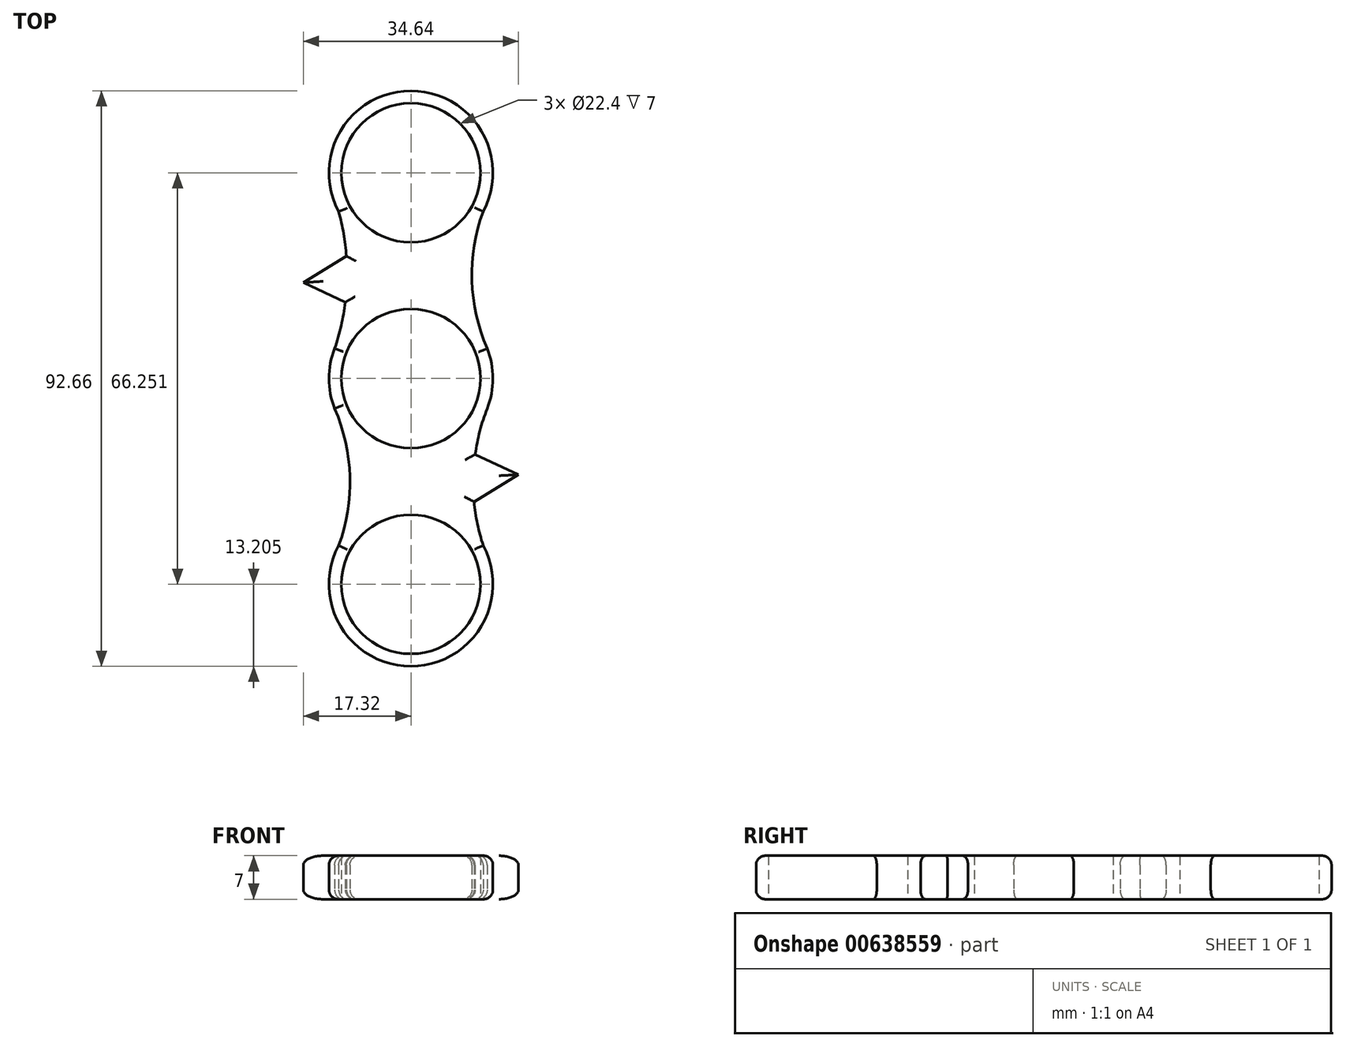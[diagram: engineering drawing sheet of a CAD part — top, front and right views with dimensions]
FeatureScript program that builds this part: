
annotation { "Feature Type Name" : "Feature", "Feature Type Description" : "" }
export const myFeature = defineFeature(function(context is Context, id is Id, definition is map)
    precondition{}
    {
        {
            var Q0;
            Q0=qCreatedBy(makeId("Top.planeOp"),FACE);
            var sketch = newSketch(context, id + "F0", { "sketchPlane" : qUnion([Q0])});
            skCircle(sketch, "E0", {"center": v(0, 0) * mm, "radius": 11.2 * mm});
            skArc(sketch, "E1", {"start": v(12.28, -4.84) * mm, "mid": v(13.2, 0.32) * mm, "end": v(12.03, 5.43) * mm});
            skCircle(sketch, "E2", {"center": v(0, 33.13) * mm, "radius": 11.2 * mm});
            skArc(sketch, "E3", {"start": v(11.63, 26.89) * mm, "mid": v(0, 46.33) * mm, "end": v(-11.63, 26.89) * mm});
            skArc(sketch, "E4.1.0", {"start": v(-11.63, -26.89) * mm, "mid": v(0, -46.33) * mm, "end": v(11.63, -26.89) * mm});
            skCircle(sketch, "E4.1.1", {"center": v(0, -33.13) * mm, "radius": 11.2 * mm});
            skArc(sketch, "E5", {"start": v(11.63, 26.89) * mm, "mid": v(9.83, 15.8) * mm, "end": v(12.28, 4.84) * mm});
            skArc(sketch, "E6.1.0", {"start": v(-11.63, -26.89) * mm, "mid": v(-9.83, -15.8) * mm, "end": v(-12.28, -4.84) * mm});
            skArc(sketch, "E7", {"start": v(-12.28, 4.84) * mm, "mid": v(-11.23, 8.53) * mm, "end": v(-10.57, 12.3) * mm});
            skArc(sketch, "E8", {"start": v(12.28, -4.84) * mm, "mid": v(11.1, -8.46) * mm, "end": v(10.35, -12.2) * mm});
            skArc(sketch, "E9.trimOffspring", {"start": v(-12.28, 4.84) * mm, "mid": v(-13.2, -0.32) * mm, "end": v(-12.03, -5.43) * mm});
            skLineSegment(sketch, "E10", {"start": v(10.35, -12.2) * mm, "end": v(17.32, -15.47) * mm});
            skLineSegment(sketch, "E11", {"start": v(17.32, -15.47) * mm, "end": v(10.17, -19.84) * mm});
            skLineSegment(sketch, "E12.1.0", {"start": v(-17.32, 15.47) * mm, "end": v(-10.17, 19.84) * mm});
            skLineSegment(sketch, "E12.1.1", {"start": v(-10.35, 12.2) * mm, "end": v(-17.32, 15.47) * mm});
            skArc(sketch, "E13.trimOffspring", {"start": v(10.17, -19.84) * mm, "mid": v(10.7, -23.4) * mm, "end": v(11.63, -26.89) * mm});
            skArc(sketch, "E14.trimOffspring", {"start": v(-10.38, 19.7) * mm, "mid": v(-10.83, 23.33) * mm, "end": v(-11.63, 26.89) * mm});
            skSolve(sketch);
        }
        {
            var Q0;
            Q0=makeQuery(id+"F0.imprint","IMPRINT",FACE,{"disambiguationData":[TD([[makeQuery(id+"F0.imprint","IMPRINT",EDGE,{"derivedFrom":sQuery(id+"F0.wireOp",EDGE,"E0")}),-1.0]])]});
            extrude(context, id + "F1", {"entities" : qUnion([Q0]), "depth" : 7 * mm, "offsetDistance" : 25 * mm});
        }
        {
            var Q0;
            Q0=makeQuery(id+"F1.opExtrude","CAP_EDGE",EDGE,{"disambiguationData":[OSD([sQuery(id+"F0.wireOp",EDGE,"E6.1.0")])],"isStart":false});
            var Q1;
            Q1=makeQuery(id+"F1.opExtrude","CAP_EDGE",EDGE,{"disambiguationData":[OSD([sQuery(id+"F0.wireOp",EDGE,"E9.trimOffspring")])],"isStart":false});
            var Q2;
            Q2=makeQuery(id+"F1.opExtrude","CAP_EDGE",EDGE,{"disambiguationData":[OSD([sQuery(id+"F0.wireOp",EDGE,"E7")])],"isStart":false});
            var Q3;
            Q3=makeQuery(id+"F1.opExtrude","CAP_EDGE",EDGE,{"disambiguationData":[OSD([sQuery(id+"F0.wireOp",EDGE,"E12.1.1")])],"isStart":false});
            var Q4;
            Q4=makeQuery(id+"F1.opExtrude","CAP_EDGE",EDGE,{"disambiguationData":[OSD([sQuery(id+"F0.wireOp",EDGE,"E12.1.0")])],"isStart":false});
            var Q5;
            Q5=makeQuery(id+"F1.opExtrude","CAP_EDGE",EDGE,{"disambiguationData":[OSD([sQuery(id+"F0.wireOp",EDGE,"E14.trimOffspring")])],"isStart":false});
            var Q6;
            Q6=makeQuery(id+"F1.opExtrude","CAP_EDGE",EDGE,{"disambiguationData":[OSD([sQuery(id+"F0.wireOp",EDGE,"E3")])],"isStart":false});
            var Q7;
            Q7=makeQuery(id+"F1.opExtrude","CAP_EDGE",EDGE,{"disambiguationData":[OSD([sQuery(id+"F0.wireOp",EDGE,"E5")])],"isStart":false});
            var Q8;
            Q8=makeQuery(id+"F1.opExtrude","CAP_EDGE",EDGE,{"disambiguationData":[OSD([sQuery(id+"F0.wireOp",EDGE,"E1")])],"isStart":false});
            var Q9;
            Q9=makeQuery(id+"F1.opExtrude","CAP_EDGE",EDGE,{"disambiguationData":[OSD([sQuery(id+"F0.wireOp",EDGE,"E8")])],"isStart":false});
            var Q10;
            Q10=makeQuery(id+"F1.opExtrude","CAP_EDGE",EDGE,{"disambiguationData":[OSD([sQuery(id+"F0.wireOp",EDGE,"E10")])],"isStart":false});
            var Q11;
            Q11=makeQuery(id+"F1.opExtrude","CAP_EDGE",EDGE,{"disambiguationData":[OSD([sQuery(id+"F0.wireOp",EDGE,"E11")])],"isStart":false});
            var Q12;
            Q12=makeQuery(id+"F1.opExtrude","CAP_EDGE",EDGE,{"disambiguationData":[OSD([sQuery(id+"F0.wireOp",EDGE,"E13.trimOffspring")])],"isStart":false});
            var Q13;
            Q13=makeQuery(id+"F1.opExtrude","CAP_EDGE",EDGE,{"disambiguationData":[OSD([sQuery(id+"F0.wireOp",EDGE,"E4.1.0")])],"isStart":false});
            var Q14;
            Q14=makeQuery(id+"F1.opExtrude","CAP_EDGE",EDGE,{"disambiguationData":[OSD([sQuery(id+"F0.wireOp",EDGE,"E4.1.0")])],"isStart":true});
            var Q15;
            Q15=makeQuery(id+"F1.opExtrude","CAP_EDGE",EDGE,{"disambiguationData":[OSD([sQuery(id+"F0.wireOp",EDGE,"E13.trimOffspring")])],"isStart":true});
            var Q16;
            Q16=makeQuery(id+"F1.opExtrude","CAP_EDGE",EDGE,{"disambiguationData":[OSD([sQuery(id+"F0.wireOp",EDGE,"E11")])],"isStart":true});
            var Q17;
            Q17=makeQuery(id+"F1.opExtrude","CAP_EDGE",EDGE,{"disambiguationData":[OSD([sQuery(id+"F0.wireOp",EDGE,"E1")])],"isStart":true});
            var Q18;
            Q18=makeQuery(id+"F1.opExtrude","CAP_EDGE",EDGE,{"disambiguationData":[OSD([sQuery(id+"F0.wireOp",EDGE,"E8")])],"isStart":true});
            var Q19;
            Q19=makeQuery(id+"F1.opExtrude","CAP_EDGE",EDGE,{"disambiguationData":[OSD([sQuery(id+"F0.wireOp",EDGE,"E5")])],"isStart":true});
            var Q20;
            Q20=makeQuery(id+"F1.opExtrude","CAP_EDGE",EDGE,{"disambiguationData":[OSD([sQuery(id+"F0.wireOp",EDGE,"E3")])],"isStart":true});
            var Q21;
            Q21=makeQuery(id+"F1.opExtrude","CAP_EDGE",EDGE,{"disambiguationData":[OSD([sQuery(id+"F0.wireOp",EDGE,"E6.1.0")])],"isStart":true});
            var Q22;
            Q22=makeQuery(id+"F1.opExtrude","CAP_EDGE",EDGE,{"disambiguationData":[OSD([sQuery(id+"F0.wireOp",EDGE,"E9.trimOffspring")])],"isStart":true});
            var Q23;
            Q23=makeQuery(id+"F1.opExtrude","CAP_EDGE",EDGE,{"disambiguationData":[OSD([sQuery(id+"F0.wireOp",EDGE,"E14.trimOffspring")])],"isStart":true});
            var Q24;
            Q24=makeQuery(id+"F1.opExtrude","CAP_EDGE",EDGE,{"disambiguationData":[OSD([sQuery(id+"F0.wireOp",EDGE,"E12.1.0")])],"isStart":true});
            var Q25;
            Q25=makeQuery(id+"F1.opExtrude","CAP_EDGE",EDGE,{"disambiguationData":[OSD([sQuery(id+"F0.wireOp",EDGE,"E7")])],"isStart":true});
            var Q26;
            Q26=makeQuery(id+"F1.opExtrude","CAP_EDGE",EDGE,{"disambiguationData":[OSD([sQuery(id+"F0.wireOp",EDGE,"E12.1.1")])],"isStart":true});
            var Q27;
            Q27=makeQuery(id+"F1.opExtrude","CAP_EDGE",EDGE,{"disambiguationData":[OSD([sQuery(id+"F0.wireOp",EDGE,"E10")])],"isStart":true});
            fillet(context, id + "F2", {"entities" : qUnion([Q0, Q1, Q2, Q3, Q4, Q5, Q6, Q7, Q8, Q9, Q10, Q11, Q12, Q13, Q14, Q15, Q16, Q17, Q18, Q19, Q20, Q21, Q22, Q23, Q24, Q25, Q26, Q27]), "radius" : 1.5 * mm, "tangentPropagation" : true, "allowEdgeOverflow" : false});
        }
    });
